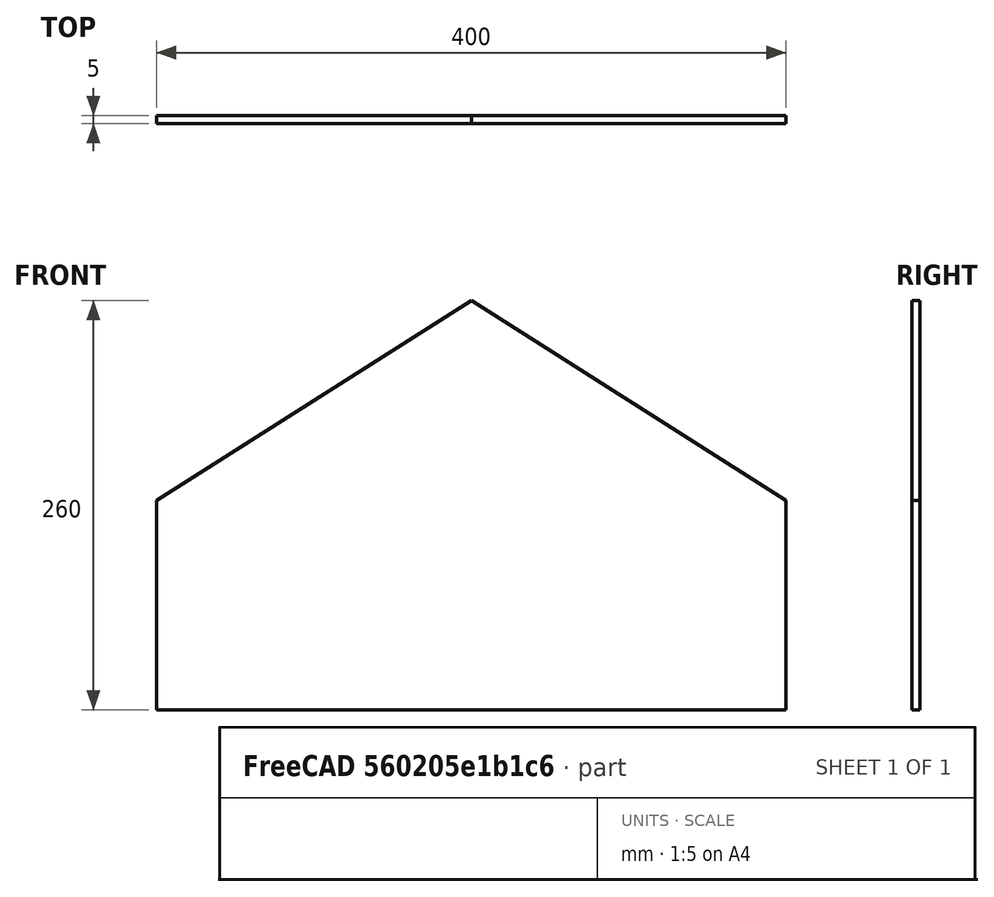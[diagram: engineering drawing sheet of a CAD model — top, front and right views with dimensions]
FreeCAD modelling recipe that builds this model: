
FCSTD DOCUMENT  (FreeCAD 0.17R11311 (Git))
Label: Rückteil2
License: All rights reserved
LicenseURL: http://en.wikipedia.org/wiki/All_rights_reserved
objects: Sketcher::SketchObject×1, PartDesign::Pad×1, PartDesign::Body×1
note: 4 computed .brp shape members not serialized (recipe doc carries the construction recipe); baked Part::Feature solids carry a one-line shape summary decoded from their .brp

FEATURE [Sketcher::SketchObject] Sketch
  MapMode = 5
  Placement = pos=(0,0,0) rot=(0,0.707107,0.707107;3.14159rad)
  Support = -> [XZ_Plane]
  sketch-geometry (5):
    g0: LineSegment StartX=200 StartY=0 StartZ=0 EndX=200 EndY=133 EndZ=0
    g1: LineSegment StartX=200 StartY=133 StartZ=0 EndX=0 EndY=260 EndZ=0
    g2: LineSegment StartX=0 StartY=260 StartZ=0 EndX=-200 EndY=133 EndZ=0
    g3: LineSegment StartX=-200 StartY=133 StartZ=0 EndX=-200 EndY=0 EndZ=0
    g4: LineSegment StartX=-200 StartY=0 StartZ=0 EndX=200 EndY=0 EndZ=0
  constraints (15):
    c: Coincident(g0,g1)
    c: Coincident(g1,g2)
    c: Coincident(g2,g3)
    c: Coincident(g3,g4)
    c: Coincident(g4,g0)
    c: PointOnObject(g3,g-1)
    c: PointOnObject(g0,g-1)
    c: Vertical(g3)
    c: Vertical(g0)
    c: Symmetric(g3,g0,g-2)
    c: PointOnObject(g1,g-2)
    c: DistanceX(g4,g4) = 400
    c: DistanceY(g3,g3) = 133
    c: Equal(g3,g0)
    c: DistanceY(g-1,g1) = 260
FEATURE [PartDesign::Pad] Pad
  BaseFeature = -> Sketch
  Length = 5
  Length2 = 100
  Placement = pos=(0,0,0) rot=(0,0.707107,0.707107;3.14159rad)
  Profile = -> Sketch
  Type = 0
FEATURE [PartDesign::Body] Body
  BaseFeature = -> Sketch
  Group = -> [Sketch,Pad]
  Origin = -> BodyOrigin
  Tip = -> Pad
